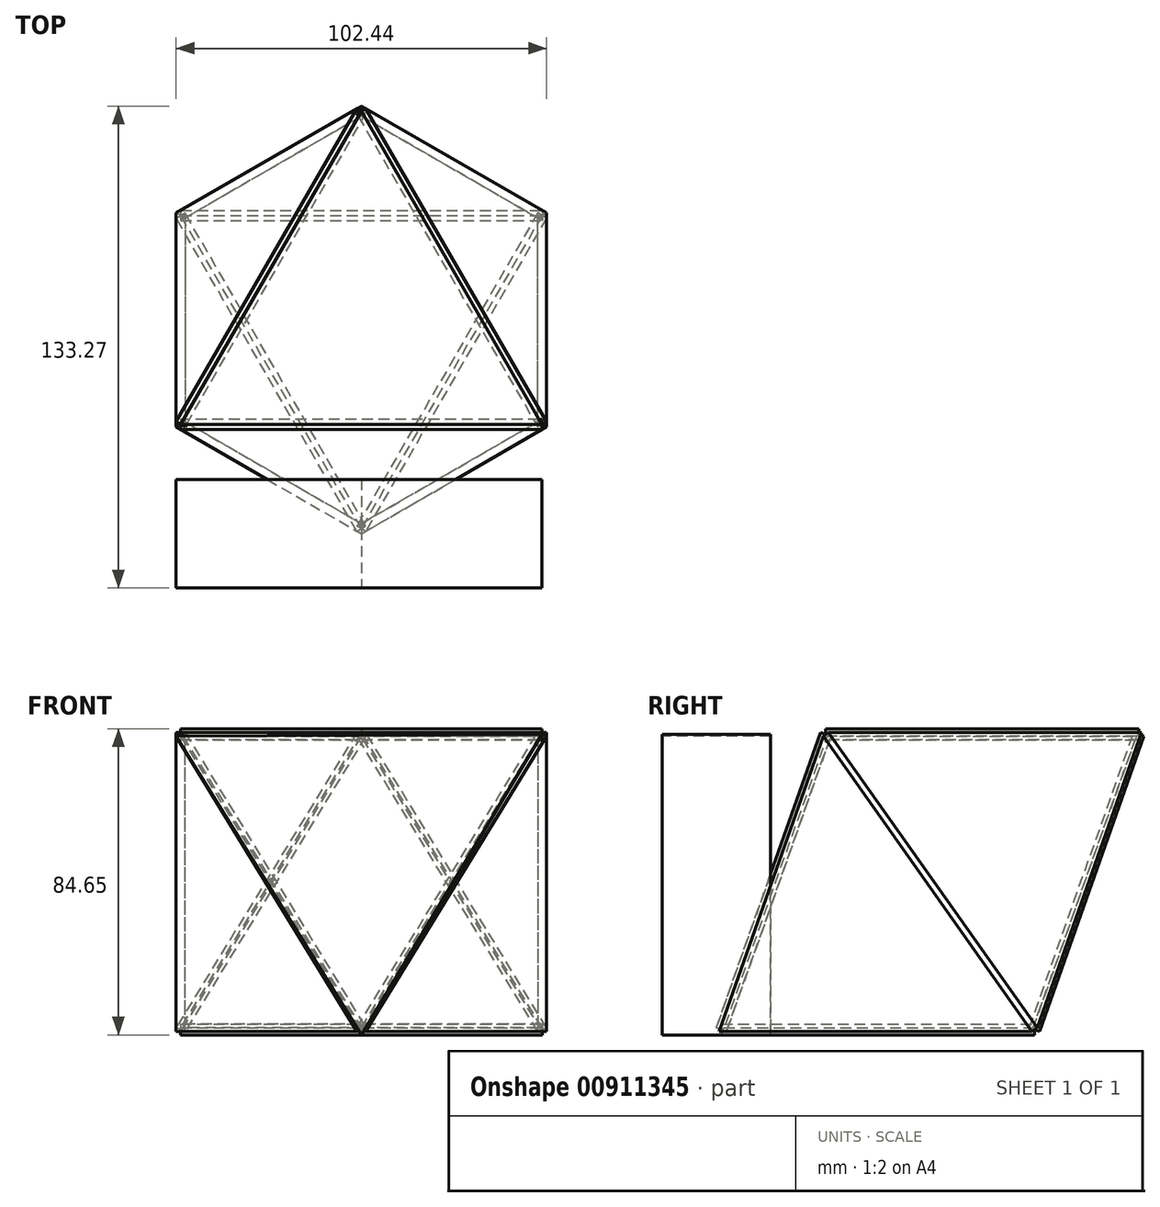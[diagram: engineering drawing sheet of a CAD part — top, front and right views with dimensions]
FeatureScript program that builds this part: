
annotation { "Feature Type Name" : "Feature", "Feature Type Description" : "" }
export const myFeature = defineFeature(function(context is Context, id is Id, definition is map)
    precondition{}
    {
        {
            var Q0;
            Q0=qCreatedBy(makeId("Top.planeOp"),FACE);
            var sketch = newSketch(context, id + "F0", { "sketchPlane" : qUnion([Q0])});
            skCircle(sketch, "E0.cCircle", {"center": v(0, 0) * mm, "radius": 28.87 * mm, "construction": true});
            skLineSegment(sketch, "E0.0", {"start": v(-50, 28.87) * mm, "end": v(50, 28.87) * mm});
            skLineSegment(sketch, "E0.1", {"start": v(50, 28.87) * mm, "end": v(0, -57.74) * mm});
            skLineSegment(sketch, "E0.2", {"start": v(0, -57.74) * mm, "end": v(-50, 28.87) * mm});
            skPoint(sketch, "E0.0.midPoint", {"position": v(0, 28.87) * mm});
            skSolve(sketch);
        }
        {
            var Q0;
            Q0=makeQuery(id+"F0.imprint","IMPRINT",FACE,{"disambiguationData":[TD([[makeQuery(id+"F0.imprint","IMPRINT",EDGE,{"derivedFrom":sQuery(id+"F0.wireOp",EDGE,"E0.0")}),-1.0]])]});
            extrude(context, id + "F1", {"entities" : qUnion([Q0]), "depth" : 3 * mm, "offsetDistance" : 25 * mm});
        }
        {
            var Q0;
            Q0=makeQuery(id+"F1.opExtrude","SWEPT_FACE",FACE,{"disambiguationData":[OSD([sQuery(id+"F0.wireOp",EDGE,"E0.2")])]});
            var sketch = newSketch(context, id + "F2", { "sketchPlane" : qUnion([Q0])});
            skLineSegment(sketch, "E1", {"start": v(-50, 1.5) * mm, "end": v(50, 1.5) * mm});
            skSolve(sketch);
        }
        {
            var Q0;
            Q0=makeQuery(id+"F1.opExtrude","SWEPT_BODY",BODY,{"disambiguationData":[OSD([sQuery(id+"F0.wireOp",EDGE,"E0.0"),sQuery(id+"F0.wireOp",EDGE,"E0.1"),sQuery(id+"F0.wireOp",EDGE,"E0.2")])]});
            transform(context, id + "F3", {"entities" : qUnion([Q0]), "transformType" : TransformType.TRANSLATION_3D, "dx" : 0 * mm, "dy" : 0 * mm, "dz" : 0 * mm, "makeCopy" : true});
        }
        {
            var Q0;
            Q0=makeQuery(id+"F3.opPattern","COPY",BODY,{"derivedFrom":makeQuery(id+"F1.opExtrude","SWEPT_BODY",BODY,{"disambiguationData":[OSD([sQuery(id+"F0.wireOp",EDGE,"E0.0"),sQuery(id+"F0.wireOp",EDGE,"E0.1"),sQuery(id+"F0.wireOp",EDGE,"E0.2")])]}),"instanceName":"1"});
            var Q1;
            Q1=sQuery(id+"F2.wireOp",EDGE,"E1");
            var Q2;
            Q2=sQuery(id+"F2.wireOp",EDGE,"E1");
            transform(context, id + "F4", {"entities" : qUnion([Q0]), "transformType" : TransformType.ROTATION, "transformAxis" : qUnion([Q2]), "angle" : 109.47 * degree, "makeCopy" : false});
        }
        {
            var Q0;
            Q0=makeQuery(id+"F1.opExtrude","SWEPT_BODY",BODY,{"disambiguationData":[OSD([sQuery(id+"F0.wireOp",EDGE,"E0.0"),sQuery(id+"F0.wireOp",EDGE,"E0.1"),sQuery(id+"F0.wireOp",EDGE,"E0.2")])]});
            transform(context, id + "F5", {"entities" : qUnion([Q0]), "transformType" : TransformType.TRANSLATION_3D, "dx" : 0 * mm, "dy" : 0 * mm, "dz" : 0 * mm, "makeCopy" : true});
        }
        {
            var Q0;
            Q0=makeQuery(id+"F1.opExtrude","SWEPT_FACE",FACE,{"disambiguationData":[OSD([sQuery(id+"F0.wireOp",EDGE,"E0.0")])]});
            var sketch = newSketch(context, id + "F6", { "sketchPlane" : qUnion([Q0])});
            skLineSegment(sketch, "E2", {"start": v(50, 1.5) * mm, "end": v(-50, 1.5) * mm});
            skSolve(sketch);
        }
        {
            var Q0;
            Q0=makeQuery(id+"F5.opPattern","COPY",BODY,{"derivedFrom":makeQuery(id+"F1.opExtrude","SWEPT_BODY",BODY,{"disambiguationData":[OSD([sQuery(id+"F0.wireOp",EDGE,"E0.0"),sQuery(id+"F0.wireOp",EDGE,"E0.1"),sQuery(id+"F0.wireOp",EDGE,"E0.2")])]}),"instanceName":"1"});
            var Q1;
            Q1=sQuery(id+"F6.wireOp",EDGE,"E2");
            var Q2;
            Q2=sQuery(id+"F6.wireOp",EDGE,"E2");
            transform(context, id + "F7", {"entities" : qUnion([Q0]), "transformType" : TransformType.ROTATION, "transformAxis" : qUnion([Q2]), "angle" : 109.47 * degree, "oppositeDirection" : true, "makeCopy" : false});
        }
        {
            var Q0;
            Q0=qCreatedBy(makeId("Front.planeOp"),FACE);
            var sketch = newSketch(context, id + "F8", { "sketchPlane" : qUnion([Q0])});
            skLineSegment(sketch, "E3", {"start": v(0, 0) * mm, "end": v(0, 75.98) * mm});
            skSolve(sketch);
        }
        {
            var Q0;
            Q0=makeQuery(id+"F3.opPattern","COPY",BODY,{"derivedFrom":makeQuery(id+"F1.opExtrude","SWEPT_BODY",BODY,{"disambiguationData":[OSD([sQuery(id+"F0.wireOp",EDGE,"E0.0"),sQuery(id+"F0.wireOp",EDGE,"E0.1"),sQuery(id+"F0.wireOp",EDGE,"E0.2")])]}),"instanceName":"1"});
            var Q1;
            Q1=sQuery(id+"F8.wireOp",EDGE,"E3");
            circularPattern(context, id + "F9", {"entities" : qUnion([Q0]), "axis" : qUnion([Q1]), "angle" : 360 * degree, "instanceCount" : 3, "equalSpace" : true});
        }
        {
            var Q0;
            Q0=makeQuery(id+"F5.opPattern","COPY",FACE,{"derivedFrom":makeQuery(id+"F1.opExtrude","SWEPT_FACE",FACE,{"disambiguationData":[OSD([sQuery(id+"F0.wireOp",EDGE,"E0.1")])]}),"instanceName":"1"});
            var sketch = newSketch(context, id + "F10", { "sketchPlane" : qUnion([Q0])});
            skLineSegment(sketch, "E4", {"start": v(21.03, -22.59) * mm, "end": v(50.3, 73.03) * mm});
            skSolve(sketch);
        }
        {
            var Q0;
            Q0=makeQuery(id+"F5.opPattern","COPY",BODY,{"derivedFrom":makeQuery(id+"F1.opExtrude","SWEPT_BODY",BODY,{"disambiguationData":[OSD([sQuery(id+"F0.wireOp",EDGE,"E0.0"),sQuery(id+"F0.wireOp",EDGE,"E0.1"),sQuery(id+"F0.wireOp",EDGE,"E0.2")])]}),"instanceName":"1"});
            var Q1;
            Q1=sQuery(id+"F10.wireOp",EDGE,"E4");
            transform(context, id + "F11", {"entities" : qUnion([Q0]), "transformType" : TransformType.ROTATION, "transformAxis" : qUnion([Q1]), "angle" : 109.47 * degree, "makeCopy" : false});
        }
        {
            var Q0;
            Q0=makeQuery(id+"F5.opPattern","COPY",BODY,{"derivedFrom":makeQuery(id+"F1.opExtrude","SWEPT_BODY",BODY,{"disambiguationData":[OSD([sQuery(id+"F0.wireOp",EDGE,"E0.0"),sQuery(id+"F0.wireOp",EDGE,"E0.1"),sQuery(id+"F0.wireOp",EDGE,"E0.2")])]}),"instanceName":"1"});
            var Q1;
            Q1=sQuery(id+"F8.wireOp",EDGE,"E3");
            circularPattern(context, id + "F12", {"entities" : qUnion([Q0]), "axis" : qUnion([Q1]), "angle" : 360 * degree, "instanceCount" : 3, "equalSpace" : true});
        }
        {
            var Q0;
            Q0=makeQuery(id+"F5.opPattern","COPY",FACE,{"derivedFrom":makeQuery(id+"F1.opExtrude","SWEPT_FACE",FACE,{"disambiguationData":[OSD([sQuery(id+"F0.wireOp",EDGE,"E0.2")])]}),"instanceName":"1"});
            var sketch = newSketch(context, id + "F13", { "sketchPlane" : qUnion([Q0])});
            skLineSegment(sketch, "E5", {"start": v(20.74, 71.33) * mm, "end": v(72.96, -13.95) * mm});
            skSolve(sketch);
        }
        {
            var Q0;
            Q0=makeQuery(id+"F5.opPattern","COPY",BODY,{"derivedFrom":makeQuery(id+"F1.opExtrude","SWEPT_BODY",BODY,{"disambiguationData":[OSD([sQuery(id+"F0.wireOp",EDGE,"E0.0"),sQuery(id+"F0.wireOp",EDGE,"E0.1"),sQuery(id+"F0.wireOp",EDGE,"E0.2")])]}),"instanceName":"1"});
            transform(context, id + "F14", {"entities" : qUnion([Q0]), "transformType" : TransformType.TRANSLATION_3D, "dx" : 0 * mm, "dy" : 0 * mm, "dz" : 0 * mm, "makeCopy" : true});
        }
        {
            var Q0;
            Q0=makeQuery(id+"F14.opPattern","COPY",BODY,{"derivedFrom":makeQuery(id+"F5.opPattern","COPY",BODY,{"derivedFrom":makeQuery(id+"F1.opExtrude","SWEPT_BODY",BODY,{"disambiguationData":[OSD([sQuery(id+"F0.wireOp",EDGE,"E0.0"),sQuery(id+"F0.wireOp",EDGE,"E0.1"),sQuery(id+"F0.wireOp",EDGE,"E0.2")])]}),"instanceName":"1"}),"instanceName":"1"});
            var Q1;
            Q1=sQuery(id+"F13.wireOp",EDGE,"E5");
            var Q2;
            Q2=sQuery(id+"F13.wireOp",EDGE,"E5");
            transform(context, id + "F15", {"entities" : qUnion([Q0]), "transformType" : TransformType.ROTATION, "transformAxis" : qUnion([Q2]), "angle" : 109.47 * degree, "oppositeDirection" : true, "makeCopy" : false});
        }
        {
            var Q0;
            Q0=qCreatedBy(makeId("Front.planeOp"),FACE);
            var sketch = newSketch(context, id + "F16", { "sketchPlane" : qUnion([Q0])});
            skLineSegment(sketch, "E6", {"start": v(-50.1, 1.05) * mm, "end": v(49.97, 83.1) * mm});
            skSolve(sketch);
        }
        {
            var Q0;
            Q0=qCreatedBy(makeId("Top.planeOp"),FACE);
            var sketch = newSketch(context, id + "F17", { "sketchPlane" : qUnion([Q0])});
            skLineSegment(sketch, "E7", {"start": v(0, -59.12) * mm, "end": v(0, 56.96) * mm});
            skSolve(sketch);
        }
        {
            var Q0;
            Q0=sQuery(id+"F17.wireOp",VERTEX,"E7.start");
            var Q1;
            Q1=sQuery(id+"F17.wireOp",EDGE,"E7");
            cPlane(context, id + "F18", {"entities" : qUnion([Q0, Q1]), "cplaneType" : CPlaneType.LINE_POINT, "offset" : 25 * mm, "width" : 150 * mm, "height" : 150 * mm});
        }
        {
            var Q0;
            Q0=qCreatedBy(id+"F18.planeOp",FACE);
            var sketch = newSketch(context, id + "F19", { "sketchPlane" : qUnion([Q0])});
            skCircle(sketch, "E8.cCircle", {"center": v(0.37, 54.48) * mm, "radius": 28.4 * mm, "construction": true});
            skLineSegment(sketch, "E8.0", {"start": v(0, 0) * mm, "end": v(-49.97, 83.1) * mm});
            skLineSegment(sketch, "E8.1", {"start": v(-49.97, 83.1) * mm, "end": v(51.22, 82.65) * mm});
            skLineSegment(sketch, "E8.2", {"start": v(51.22, 82.65) * mm, "end": v(0, 0) * mm});
            skPoint(sketch, "E8.0.midPoint", {"position": v(-26.98, 46.87) * mm});
            skSolve(sketch);
        }
        {
            var Q0;
            Q0=makeQuery(id+"F19.imprint","IMPRINT",FACE,{"disambiguationData":[TD([[makeQuery(id+"F19.imprint","IMPRINT",EDGE,{"derivedFrom":sQuery(id+"F19.wireOp",EDGE,"E8.0")}),-1.0]])]});
            extrude(context, id + "F20", {"entities" : qUnion([Q0]), "depth" : 15 * mm, "offsetDistance" : 25 * mm, "hasSecondDirection" : true, "secondDirectionOppositeDirection" : true, "secondDirectionDepth" : 15 * mm});
        }
    });
